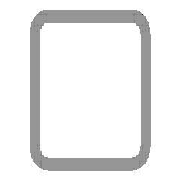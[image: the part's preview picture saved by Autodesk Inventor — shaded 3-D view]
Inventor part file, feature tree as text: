
AUTODESK INVENTOR PART (.ipt)
format: ipt  version: 2025 (Build 290162010, 162A)  size: 133,632 bytes
history: native  units: mm (DEFAULTED — no unit token found)
features: other x4, sketch x1, plane x1
ambient origin geometry x8: Origin, YZ Plane, XZ Plane, XY Plane, X Axis, Y Axis, Z Axis, Center Point
bodies: Solid1 (feature_tree), Body (feature_tree)
feature tree (6):
  parser-record x1  (decoder bookkeeping rows leaked as tree rows — omitted from the tree; the rows remain in map.json)
  other  "Driven Length"
  other  "Start Plane"
  other  "End Plane"
  sketch  "Sketch3"  dims[d3=1371.779787mm d4=0.0mm d7=6.0mm d9=80.0mm d11=80.0mm d12=3.0mm d13=40.0mm d14=1411.779787mm d15=40.0mm d16=40.0mm d17=90.0deg d18=1371.779787mm]
  plane  "Work Plane3"
